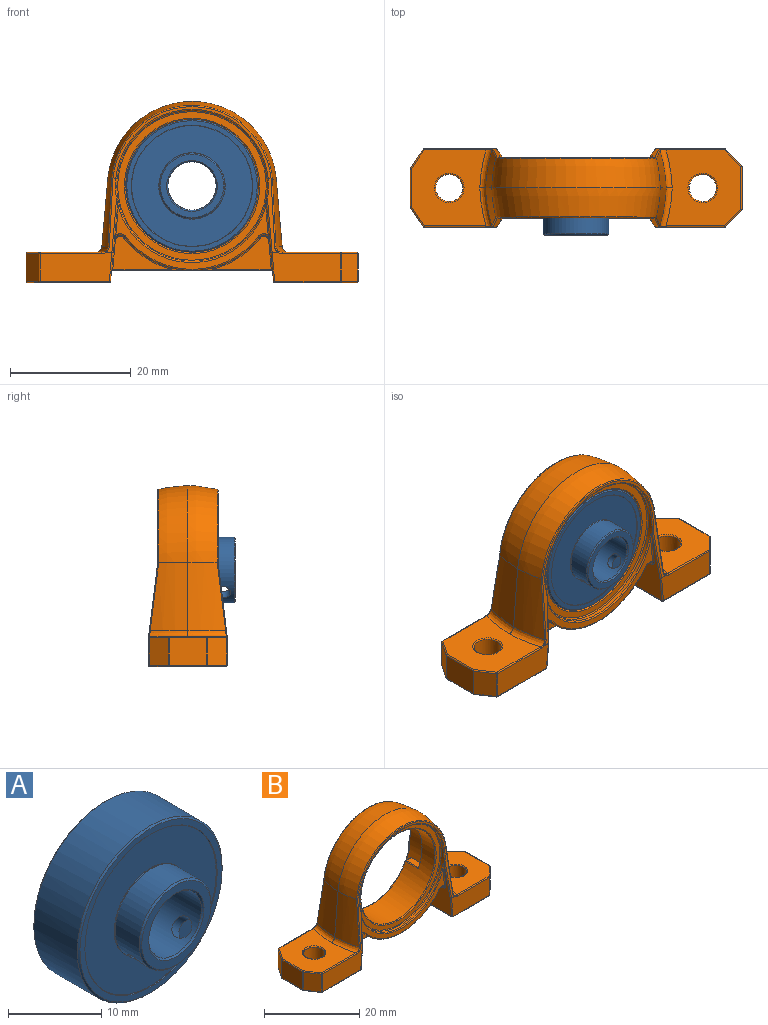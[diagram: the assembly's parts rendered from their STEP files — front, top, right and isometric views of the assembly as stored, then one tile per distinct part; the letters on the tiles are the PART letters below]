
ASSEMBLY  parts=2 mates=1
PART A: 24 faces, bbox 22x10.9x22 mm
  f0: plane 20x20mm, normal (0,1,0), area 219.1mm2, adj f5,f9
  f1: cylinder r=11mm len=22mm, axis (0,1,0), area 456.2mm2, adj f22,f23
  f2: plane 21.6x21.6mm, normal (0,-1,0), area 49.1mm2, adj f6,f22
  f3: plane 21.6x21.6mm, normal (0,1,0), area 49.1mm2, adj f4,f23
  f4: cone r=10.05mm half-angle=45deg, axis (0,1,0), area 4.5mm2, adj f3,f5
  f5: cylinder r=10mm len=20mm, axis (0,1,0), area 3.1mm2, adj f0,f4
  f6: cone r=10.05mm half-angle=45deg, axis (0,-1,0), area 4.5mm2, adj f2,f7
  f7: cylinder r=10mm len=20mm, axis (0,-1,0), area 3.1mm2, adj f6,f8
  f8: plane 20x20mm, normal (0,-1,0), area 219.1mm2, adj f7,f12
  f9: cylinder r=5.5mm len=11mm, axis (0,-1,0), area 1.7mm2, adj f0,f10
  f10: cone r=5.5mm half-angle=45deg, axis (0,-1,0), area 2.4mm2, adj f9,f11
  f11: plane 10.9x10.9mm, normal (0,1,0), area 37.9mm2, adj f10,f19
  f12: cylinder r=5.5mm len=11mm, axis (0,-1,0), area 1.7mm2, adj f8,f15
  f13: plane 10.5x10.5mm, normal (0,-1,0), area 31.2mm2, adj f20,f21
  f14: cylinder r=5.45mm len=10.9mm, axis (0,-1,0), area 115.1mm2, adj f15,f17,f18,f20
  f15: cone r=5.45mm half-angle=45deg, axis (0,1,0), area 2.4mm2, adj f12,f14
  f16: cylinder r=4mm len=10.45mm, axis (0,-1,0), area 252.7mm2, adj f17,f18,f19,f21
  f17: cylinder r=1.25mm len=2.95mm, axis (-0.72,0,-0.69), area 11.6mm2, adj f14,f16
  f18: cylinder r=1.25mm len=2.95mm, axis (0.72,0,-0.69), area 11.6mm2, adj f14,f16
  f19: cone r=4.2mm half-angle=45deg, axis (0,1,0), area 7.3mm2, adj f11,f16
  f20: cone r=5.25mm half-angle=45deg, axis (0,1,0), area 9.5mm2, adj f13,f14
  f21: cone r=4mm half-angle=45deg, axis (0,-1,0), area 7.3mm2, adj f13,f16
  f22: cone r=11mm half-angle=45deg, axis (0,1,0), area 19.4mm2, adj f1,f2
  f23: cone r=10.8mm half-angle=45deg, axis (0,-1,0), area 19.4mm2, adj f1,f3
PART B: 247 faces, bbox 55.2x14x30.2 mm
  f0: plane 22.96x7.55mm, normal (0,1,0), area 35.1mm2, adj f36,f150,f153,f155
  f1: plane 13.6x12.6mm, normal (0,0,-1), area 145.8mm2, adj f133,f134,f135,f136,f137,f138,f139
  f2: plane 12.6x12.38mm, normal (0,0,1), area 122.3mm2, adj f57,f58,f118,f119,f120,f121,f122,f147
  f3: plane 11.31x4.79mm, normal (0,1,0), area 51.3mm2, adj f124,f125,f145,f196,f202,f233
  f4: plane 11.9x4.79mm, normal (0,1,0), area 54mm2, adj f117,f118,f135,f195,f199,f230
  f5: plane 13.6x12.6mm, normal (0,0,-1), area 145.2mm2, adj f140,f141,f142,f143,f144,f145,f146
  f6: plane 7.18x4.6mm, normal (1,0,0), area 33mm2, adj f127,f141,f236,f239
  f7: plane 12.6x12.38mm, normal (0,0,1), area 121.7mm2, adj f55,f56,f125,f126,f127,f128,f129,f148
  f8: plane 6.22x4.6mm, normal (-1,0,0), area 28.6mm2, adj f120,f138,f224,f227
  f9: plane 26.19x11.92mm, normal (0,1,0), area 17mm2, adj f209,f217,f218,f222
  f10: plane 12.19x1.74mm, normal (0,0.99,0.12), area 7.6mm2, adj f199,f200,f207,f208,f212,f217
  f11: plane 12.19x1.74mm, normal (0,0.99,0.12), area 7.6mm2, adj f201,f202,f210,f211,f215,f218,f219
  f12: cylinder r=14mm len=22.23mm, axis (0,-1,0), area 92.4mm2, adj f51,f53,f64,f65,f69,f70,f107
  f13: plane 13.76x12.77mm, normal (-1,0,-0.09), area 79.2mm2, adj f51,f52,f74,f78,f80,f81,f84,f94
  f14: plane 13.76x12.77mm, normal (1,0,-0.09), area 79.2mm2, adj f53,f54,f77,f79,f82,f85,f89,f100
  f15: plane 25.25x10.33mm, normal (0,1,0), area 37.6mm2, adj f105,f107,f109,f110,f113,f114
  f16: cylinder r=11mm len=22mm, axis (0,1,0), area 448.7mm2, adj f47,f50,f132,f149,f152,f153,f157,f160
  f17: plane 26.19x11.92mm, normal (0,-1,0), area 17mm2, adj f179,f187,f188,f192
  f18: plane 11.31x4.79mm, normal (0,-1,0), area 51.3mm2, adj f129,f130,f144,f165,f169,f242
  f19: plane 11.9x4.79mm, normal (0,-1,0), area 54mm2, adj f122,f123,f134,f166,f172,f245
  f20: plane 12.19x1.74mm, normal (0,-0.99,0.12), area 7.6mm2, adj f171,f172,f180,f181,f185,f188
  f21: plane 12.19x1.74mm, normal (0,-0.99,0.12), area 7.6mm2, adj f169,f170,f177,f178,f182,f186,f187
  f22: cylinder r=14mm len=22.23mm, axis (0,1,0), area 92.4mm2, adj f52,f54,f62,f63,f86,f92,f95
  f23: plane 25.25x10.33mm, normal (0,-1,0), area 37.6mm2, adj f93,f95,f97,f98,f101,f102
  f24: cylinder r=12.5mm len=25mm, axis (0,-1,0), area 48.8mm2, adj f96,f99,f101,f103,f104,f131,f178,f179
  f25: plane 24.6x24.6mm, normal (0,-1,0), area 81.2mm2, adj f131,f132
  f26: plane 26.31x1.6mm, normal (0,0,-1), area 42.1mm2, adj f59,f60,f67,f68,f75,f76,f81,f82
  f27: plane 9.77x5.48mm, normal (0,-1,0), area 24mm2, adj f88,f89,f91,f92
  f28: plane 9.77x5.48mm, normal (0,-1,0), area 24mm2, adj f80,f83,f86,f87
  f29: cylinder r=25.08mm len=11.46mm, axis (-0.09,0,-1), area 63.8mm2, adj f31,f40,f57,f185,f189
  f30: cylinder r=25.08mm len=11.4mm, axis (-0.09,0,1), area 63.5mm2, adj f31,f41,f55,f182
  f31: revolved ~27.89x12.9mm, area 199.8mm2, adj f29,f30,f42,f186,f190,f191,f192
  f32: cylinder r=2.25mm len=4.6mm, axis (0,0,1), area 65mm2, adj f139,f147
  f33: plane 4.6x3.19mm, normal (-0.83,-0.55,0), area 17.6mm2, adj f121,f136,f224,f245
  f34: plane 4.6x2.71mm, normal (0.71,-0.71,0), area 17.6mm2, adj f128,f142,f239,f242
  f35: cylinder r=2.25mm len=4.6mm, axis (0,0,1), area 65mm2, adj f140,f148
  f36: cylinder r=12.5mm len=25mm, axis (0,1,0), area 142.5mm2, adj f0,f37,f45,f46,f47,f48,f49,f50
  f37: plane 22.96x7.55mm, normal (0,1,0), area 35.1mm2, adj f36,f156,f159,f160
  f38: plane 9.77x5.48mm, normal (0,1,0), area 24mm2, adj f70,f73,f76,f77
  f39: plane 9.77x5.48mm, normal (0,1,0), area 24mm2, adj f69,f71,f74,f75
  f40: cylinder r=25.09mm len=11.46mm, axis (-0.09,0,-1), area 63.8mm2, adj f29,f42,f58,f212,f216
  f41: cylinder r=25.09mm len=11.4mm, axis (-0.09,0,1), area 63.5mm2, adj f30,f42,f56,f215
  f42: revolved ~27.89x12.9mm, area 199.8mm2, adj f31,f40,f41,f219,f220,f221,f222
  f43: plane 4.6x3.19mm, normal (-0.83,0.55,0), area 17.6mm2, adj f119,f137,f227,f230
  f44: plane 4.6x2.71mm, normal (0.71,0.71,0), area 17.6mm2, adj f126,f143,f233,f236
  f45: plane 3.8x1.52mm, normal (0,0,-1), area 5.8mm2, adj f36,f47,f152,f155
  f46: plane 3.8x1.52mm, normal (0,0,1), area 5.8mm2, adj f36,f47,f159,f162
  f47: plane 9.72x2.63mm, normal (0,1,0), area 14.7mm2, adj f16,f36,f45,f46,f152,f162
  f48: plane 3.8x1.52mm, normal (0,0,-1), area 5.8mm2, adj f36,f50,f149,f150
  f49: plane 3.8x1.52mm, normal (0,0,1), area 5.8mm2, adj f36,f50,f156,f157
  f50: plane 9.72x2.63mm, normal (0,1,0), area 14.7mm2, adj f16,f36,f48,f49,f149,f157
  f51: cylinder r=1mm len=3.6mm, axis (0,-1,0), area 8.6mm2, adj f12,f13,f71,f110
  f52: cylinder r=1mm len=3.6mm, axis (0,1,0), area 8.6mm2, adj f13,f22,f83,f93
  f53: cylinder r=1mm len=3.6mm, axis (0,-1,0), area 8.6mm2, adj f12,f14,f73,f105
  f54: cylinder r=1mm len=3.6mm, axis (0,1,0), area 8.6mm2, adj f14,f22,f91,f98
  f55: bspline ~11.42x2.29mm, area 9.5mm2, adj f7,f30,f56,f130,f177
  f56: bspline ~7.28x2.2mm, area 9.5mm2, adj f7,f41,f55,f124,f211
  f57: bspline ~11.42x2.29mm, area 9.5mm2, adj f2,f29,f58,f123,f181
  f58: bspline ~8.05x2.18mm, area 9.5mm2, adj f2,f40,f57,f117,f207
  f59: bspline ~3.35x0.2mm, area 0.6mm2, adj f26,f60,f88,f90
  f60: bspline ~3.35x0.2mm, area 0.6mm2, adj f26,f59,f61,f87
  f61: bspline ~3.35x0.34mm, area 0.4mm2, adj f60,f62,f86,f87
  f62: bspline ~3.31x0.39mm, area 0.5mm2, adj f22,f61,f63,f86
  f63: bspline ~3.31x0.39mm, area 0.5mm2, adj f22,f62,f90,f92
  f64: bspline ~3.31x0.39mm, area 0.5mm2, adj f12,f65,f70,f72
  f65: bspline ~3.31x0.39mm, area 0.5mm2, adj f12,f64,f66,f69
  f66: bspline ~3.35x0.34mm, area 0.4mm2, adj f65,f67,f69,f75
  f67: bspline ~3.35x0.2mm, area 0.6mm2, adj f26,f66,f68,f75
  f68: bspline ~3.35x0.2mm, area 0.6mm2, adj f26,f67,f72,f76
  f69: torus R=14.2mm, axis (0,-1,0), area 3mm2, adj f12,f39,f65,f66,f71
  f70: torus R=14.2mm, axis (0,-1,0), area 3mm2, adj f12,f38,f64,f72,f73
  f71: torus R=0.8mm, axis (0,-1,0), area 0.7mm2, adj f39,f51,f69,f74
  f72: bspline ~3.35x0.34mm, area 0.4mm2, adj f64,f68,f70,f76
  f73: torus R=0.8mm, axis (0,-1,0), area 0.7mm2, adj f38,f53,f70,f77
  f74: cylinder r=0.2mm len=4.76mm, axis (0.09,0,-1), area 1.5mm2, adj f13,f39,f71,f78
  f75: cylinder r=0.2mm len=9.81mm, axis (1,0,0), area 3.1mm2, adj f26,f39,f66,f67,f78
  f76: cylinder r=0.2mm len=9.81mm, axis (1,0,0), area 3.1mm2, adj f26,f38,f68,f72,f79
  f77: cylinder r=0.2mm len=4.76mm, axis (-0.09,0,-1), area 1.5mm2, adj f14,f38,f73,f79
  f78: bspline ~0.4x0.4mm, area 0.1mm2, adj f13,f74,f75,f81
  f79: bspline ~0.47x0.47mm, area 0.1mm2, adj f14,f76,f77,f82
  f80: cylinder r=0.2mm len=4.76mm, axis (0.09,0,-1), area 1.5mm2, adj f13,f28,f83,f84
  f81: cylinder r=0.2mm len=1.6mm, axis (0,1,0), area 0.5mm2, adj f13,f26,f78,f84
  f82: cylinder r=0.2mm len=1.6mm, axis (0,-1,0), area 0.5mm2, adj f14,f26,f79,f85
  f83: torus R=0.8mm, axis (0,1,0), area 0.7mm2, adj f28,f52,f80,f86
  f84: bspline ~0.5x0.4mm, area 0.1mm2, adj f13,f80,f81,f87
  f85: bspline ~0.47x0.42mm, area 0.1mm2, adj f14,f82,f88,f89
  f86: torus R=14.2mm, axis (0,1,0), area 3mm2, adj f22,f28,f61,f62,f83
  f87: cylinder r=0.2mm len=9.81mm, axis (1,0,0), area 3.1mm2, adj f26,f28,f60,f61,f84
  f88: cylinder r=0.2mm len=9.81mm, axis (1,0,0), area 3.1mm2, adj f26,f27,f59,f85,f90
  f89: cylinder r=0.2mm len=4.76mm, axis (-0.09,0,-1), area 1.5mm2, adj f14,f27,f85,f91
  f90: bspline ~3.35x0.34mm, area 0.4mm2, adj f59,f63,f88,f92
  f91: torus R=0.8mm, axis (0,1,0), area 0.7mm2, adj f27,f54,f89,f92
  f92: torus R=14.2mm, axis (0,1,0), area 3mm2, adj f22,f27,f63,f90,f91
  f93: torus R=1.2mm, axis (0,-1,0), area 0.7mm2, adj f23,f52,f94,f95
  f94: bspline ~1.03x0.4mm, area 0.1mm2, adj f13,f93,f97
  f95: torus R=13.8mm, axis (0,-1,0), area 8mm2, adj f22,f23,f93,f98
  f96: cylinder r=0.2mm len=0.05mm, axis (0,-1,0), area 0mm2, adj f13,f24,f99,f174
  f97: cylinder r=0.2mm len=5.94mm, axis (-0.09,0,1), area 1.7mm2, adj f13,f23,f94,f99
  f98: torus R=1.2mm, axis (0,-1,0), area 0.7mm2, adj f23,f54,f95,f100
  f99: bspline ~1.39x0.42mm, area 0.3mm2, adj f24,f96,f97,f101
  f100: bspline ~1.03x0.4mm, area 0.1mm2, adj f14,f98,f102
  f101: torus R=12.7mm, axis (0,-1,0), area 10.2mm2, adj f23,f24,f99,f103
  f102: cylinder r=0.2mm len=5.94mm, axis (-0.09,0,-1), area 1.7mm2, adj f14,f23,f100,f103
  f103: bspline ~1.39x0.43mm, area 0.3mm2, adj f24,f101,f102,f104
  f104: cylinder r=0.2mm len=0.05mm, axis (0,-1,0), area 0mm2, adj f14,f24,f103,f175
  f105: torus R=1.2mm, axis (0,1,0), area 0.7mm2, adj f15,f53,f106,f107
  f106: bspline ~1.03x0.4mm, area 0.1mm2, adj f14,f105,f109
  f107: torus R=13.8mm, axis (0,1,0), area 8mm2, adj f12,f15,f105,f110
  f108: cylinder r=0.2mm len=0.05mm, axis (0,1,0), area 0mm2, adj f14,f36,f111,f204
  f109: cylinder r=0.2mm len=5.94mm, axis (-0.09,0,-1), area 1.7mm2, adj f14,f15,f106,f111
  f110: torus R=1.2mm, axis (0,1,0), area 0.7mm2, adj f15,f51,f107,f112
  f111: bspline ~1.39x0.42mm, area 0.3mm2, adj f36,f108,f109,f113
  f112: bspline ~1.03x0.4mm, area 0.1mm2, adj f13,f110,f114
  f113: torus R=12.7mm, axis (0,1,0), area 10.2mm2, adj f15,f36,f111,f115
  f114: cylinder r=0.2mm len=5.94mm, axis (-0.09,0,1), area 1.7mm2, adj f13,f15,f112,f115
  f115: bspline ~1.39x0.43mm, area 0.3mm2, adj f36,f113,f114,f116
  f116: cylinder r=0.2mm len=0.05mm, axis (0,1,0), area 0mm2, adj f13,f36,f115,f205
  f117: bspline ~1.15x0.47mm, area 0.2mm2, adj f4,f58,f118,f203
  f118: cylinder r=0.2mm len=10.25mm, axis (-1,0,0), area 3.2mm2, adj f2,f4,f117,f229
  f119: cylinder r=0.2mm len=3.3mm, axis (0.55,0.83,0), area 1.2mm2, adj f2,f43,f226,f229
  f120: cylinder r=0.2mm len=6.22mm, axis (0,1,0), area 2mm2, adj f2,f8,f223,f226
  f121: cylinder r=0.2mm len=3.3mm, axis (-0.55,0.83,0), area 1.2mm2, adj f2,f33,f223,f244
  f122: cylinder r=0.2mm len=10.25mm, axis (-1,0,0), area 3.2mm2, adj f2,f19,f123,f244
  f123: bspline ~1.15x0.47mm, area 0.2mm2, adj f19,f57,f122,f176
  f124: bspline ~1.15x0.47mm, area 0.2mm2, adj f3,f56,f125,f206
  f125: cylinder r=0.2mm len=9.67mm, axis (-1,0,0), area 3mm2, adj f3,f7,f124,f232
  f126: cylinder r=0.2mm len=2.85mm, axis (-0.71,0.71,0), area 1.2mm2, adj f7,f44,f232,f235
  f127: cylinder r=0.2mm len=7.18mm, axis (0,1,0), area 2.3mm2, adj f6,f7,f235,f238
  f128: cylinder r=0.2mm len=2.85mm, axis (0.71,0.71,0), area 1.2mm2, adj f7,f34,f238,f241
  f129: cylinder r=0.2mm len=9.67mm, axis (-1,0,0), area 3mm2, adj f7,f18,f130,f241
  f130: bspline ~1.15x0.47mm, area 0.2mm2, adj f18,f55,f129,f173
  f131: torus R=12.3mm, axis (0,-1,0), area 24.5mm2, adj f24,f25
  f132: torus R=11.2mm, axis (0,-1,0), area 21.9mm2, adj f16,f25
  f133: cylinder r=0.2mm len=12.6mm, axis (0,-1,0), area 3.7mm2, adj f1,f14,f164,f193
  f134: cylinder r=0.2mm len=11.48mm, axis (1,0,0), area 3.6mm2, adj f1,f19,f164,f246
  f135: cylinder r=0.2mm len=11.48mm, axis (1,0,0), area 3.6mm2, adj f1,f4,f193,f231
  f136: cylinder r=0.2mm len=3.3mm, axis (-0.55,0.83,0), area 1.2mm2, adj f1,f33,f225,f246
  f137: cylinder r=0.2mm len=3.3mm, axis (0.55,0.83,0), area 1.2mm2, adj f1,f43,f228,f231
  f138: cylinder r=0.2mm len=6.22mm, axis (0,1,0), area 2mm2, adj f1,f8,f225,f228
  f139: torus R=2.45mm, axis (0,0,1), area 4.6mm2, adj f1,f32
  f140: torus R=2.45mm, axis (0,0,-1), area 4.6mm2, adj f5,f35
  f141: cylinder r=0.2mm len=7.18mm, axis (0,1,0), area 2.3mm2, adj f5,f6,f237,f240
  f142: cylinder r=0.2mm len=2.85mm, axis (0.71,0.71,0), area 1.2mm2, adj f5,f34,f240,f243
  f143: cylinder r=0.2mm len=2.85mm, axis (-0.71,0.71,0), area 1.2mm2, adj f5,f44,f234,f237
  f144: cylinder r=0.2mm len=10.89mm, axis (1,0,0), area 3.4mm2, adj f5,f18,f163,f243
  f145: cylinder r=0.2mm len=10.89mm, axis (1,0,0), area 3.4mm2, adj f3,f5,f194,f234
  f146: cylinder r=0.2mm len=12.6mm, axis (0,-1,0), area 3.7mm2, adj f5,f13,f163,f194
  f147: torus R=2.45mm, axis (0,0,-1), area 4.6mm2, adj f2,f32
  f148: torus R=2.45mm, axis (0,0,1), area 4.6mm2, adj f7,f35
  f149: cylinder r=0.2mm len=3.8mm, axis (0,1,0), area 0.8mm2, adj f16,f48,f50,f151
  f150: cylinder r=0.2mm len=1.52mm, axis (-1,0,0), area 0.5mm2, adj f0,f36,f48,f151
  f151: sphere r=0.2mm, area 0mm2, adj f149,f150,f153
  f152: cylinder r=0.2mm len=3.8mm, axis (0,1,0), area 0.8mm2, adj f16,f45,f47,f154
  f153: torus R=11.2mm, axis (0,1,0), area 7.7mm2, adj f0,f16,f151,f154
  f154: sphere r=0.2mm, area 0mm2, adj f152,f153,f155
  f155: cylinder r=0.2mm len=1.52mm, axis (-1,0,0), area 0.5mm2, adj f0,f36,f45,f154
  f156: cylinder r=0.2mm len=1.52mm, axis (1,0,0), area 0.5mm2, adj f36,f37,f49,f158
  f157: cylinder r=0.2mm len=3.8mm, axis (0,1,0), area 0.8mm2, adj f16,f49,f50,f158
  f158: sphere r=0.2mm, area 0mm2, adj f156,f157,f160
  f159: cylinder r=0.2mm len=1.52mm, axis (1,0,0), area 0.5mm2, adj f36,f37,f46,f161
  f160: torus R=11.2mm, axis (0,1,0), area 7.7mm2, adj f16,f37,f158,f161
  f161: sphere r=0.2mm, area 0mm2, adj f159,f160,f162
  f162: cylinder r=0.2mm len=3.8mm, axis (0,1,0), area 0.8mm2, adj f16,f46,f47,f161
  f163: sphere r=0.2mm, area 0.1mm2, adj f144,f146,f165
  f164: sphere r=0.2mm, area 0.1mm2, adj f133,f134,f166
  f165: cylinder r=0.2mm len=4.81mm, axis (0.09,0,-1), area 1.5mm2, adj f13,f18,f163,f167
  f166: cylinder r=0.2mm len=4.81mm, axis (0.09,0,1), area 1.5mm2, adj f14,f19,f164,f168
  f167: sphere r=0.2mm, area 0mm2, adj f165,f169,f170
  f168: sphere r=0.2mm, area 0mm2, adj f166,f171,f172
  f169: cylinder r=0.2mm len=0.97mm, axis (-1,0,0), area 0mm2, adj f18,f21,f167,f173
  f170: cylinder r=0.2mm len=8.84mm, axis (-0.09,0.12,0.99), area 2.8mm2, adj f13,f21,f167,f174
  f171: cylinder r=0.2mm len=8.84mm, axis (-0.09,-0.12,-0.99), area 2.8mm2, adj f14,f20,f168,f175
  f172: cylinder r=0.2mm len=0.97mm, axis (1,0,0), area 0mm2, adj f19,f20,f168,f176
  f173: sphere r=0.2mm, area 0mm2, adj f130,f169,f177
  f174: sphere r=0.2mm, area 0mm2, adj f96,f170,f178
  f175: sphere r=0.2mm, area 0mm2, adj f104,f171,f180
  f176: sphere r=0.2mm, area 0mm2, adj f123,f172,f181
  f177: bspline ~1.15x0.73mm, area 0.3mm2, adj f21,f55,f173,f182
  f178: bspline ~3.39x0.62mm, area 1.1mm2, adj f21,f24,f174,f183
  f179: torus R=12.7mm, axis (0,-1,0), area 11.6mm2, adj f17,f24,f183,f184
  f180: bspline ~3.39x0.62mm, area 1.1mm2, adj f20,f24,f175,f184
  f181: bspline ~1.13x0.79mm, area 0.3mm2, adj f20,f57,f176,f185
  f182: bspline ~13.27x1.78mm, area 2.9mm2, adj f21,f30,f177,f186
  f183: bspline ~0.22x0.22mm, area 0mm2, adj f24,f178,f179,f187
  f184: bspline ~0.22x0.21mm, area 0mm2, adj f24,f179,f180,f188
  f185: bspline ~13.27x1.78mm, area 3mm2, adj f20,f29,f181,f189
  f186: bspline ~3.79x0.63mm, area 0mm2, adj f21,f31,f182,f190
  f187: cylinder r=0.2mm len=0.45mm, axis (1,0,0), area 0mm2, adj f17,f21,f183,f190
  f188: cylinder r=0.2mm len=0.45mm, axis (1,0,0), area 0mm2, adj f17,f20,f184,f189,f191
  f189: bspline ~0.2x0.16mm, area 0mm2, adj f29,f185,f188,f191
  f190: bspline ~0.21x0.17mm, area 0mm2, adj f31,f186,f187,f192
  f191: bspline ~0.21x0.18mm, area 0mm2, adj f31,f188,f189,f192
  f192: bspline ~26.56x12.1mm, area 10.5mm2, adj f17,f31,f190,f191
  f193: sphere r=0.2mm, area 0mm2, adj f133,f135,f195
  f194: sphere r=0.2mm, area 0.1mm2, adj f145,f146,f196
  f195: cylinder r=0.2mm len=4.81mm, axis (0.09,0,1), area 1.5mm2, adj f4,f14,f193,f197
  f196: cylinder r=0.2mm len=4.81mm, axis (0.09,0,-1), area 1.5mm2, adj f3,f13,f194,f198
  f197: sphere r=0.2mm, area 0mm2, adj f195,f199,f200
  f198: sphere r=0.2mm, area 0mm2, adj f196,f201,f202
  f199: cylinder r=0.2mm len=0.97mm, axis (1,0,0), area 0mm2, adj f4,f10,f197,f203
  f200: cylinder r=0.2mm len=8.84mm, axis (-0.09,0.12,-0.99), area 2.8mm2, adj f10,f14,f197,f204
  f201: cylinder r=0.2mm len=8.84mm, axis (-0.09,-0.12,0.99), area 2.8mm2, adj f11,f13,f198,f205
  f202: cylinder r=0.2mm len=0.97mm, axis (-1,0,0), area 0mm2, adj f3,f11,f198,f206
  f203: sphere r=0.2mm, area 0mm2, adj f117,f199,f207
  f204: sphere r=0.2mm, area 0mm2, adj f108,f200,f208
  f205: sphere r=0.2mm, area 0mm2, adj f116,f201,f210
  f206: sphere r=0.2mm, area 0mm2, adj f124,f202,f211
  f207: bspline ~1.15x0.73mm, area 0.3mm2, adj f10,f58,f203,f212
  f208: bspline ~3.39x0.62mm, area 1.1mm2, adj f10,f36,f204,f213
  f209: torus R=12.7mm, axis (0,1,0), area 11.6mm2, adj f9,f36,f213,f214
  f210: bspline ~3.39x0.62mm, area 1.1mm2, adj f11,f36,f205,f214
  f211: bspline ~1.13x0.79mm, area 0.3mm2, adj f11,f56,f206,f215
  f212: bspline ~13.27x1.78mm, area 3mm2, adj f10,f40,f207,f216
  f213: bspline ~0.22x0.22mm, area 0mm2, adj f36,f208,f209,f217
  f214: bspline ~0.22x0.21mm, area 0mm2, adj f36,f209,f210,f218
  f215: bspline ~11.2x1.53mm, area 2.9mm2, adj f11,f41,f211,f219
  f216: bspline ~0.2x0.16mm, area 0mm2, adj f40,f212,f217,f220
  f217: cylinder r=0.2mm len=0.45mm, axis (-1,0,0), area 0mm2, adj f9,f10,f213,f216,f220
  f218: cylinder r=0.2mm len=0.45mm, axis (-1,0,0), area 0mm2, adj f9,f11,f214,f221
  f219: bspline ~3.79x0.63mm, area 0mm2, adj f11,f42,f215,f221
  f220: bspline ~0.21x0.18mm, area 0mm2, adj f42,f216,f217,f222
  f221: bspline ~0.2x0.17mm, area 0mm2, adj f42,f218,f219,f222
  f222: bspline ~26.66x12.66mm, area 10.5mm2, adj f9,f42,f220,f221
  f223: sphere r=0.2mm, area 0mm2, adj f120,f121,f224
  f224: cylinder r=0.2mm len=4.6mm, axis (0,0,1), area 0.5mm2, adj f8,f33,f223,f225
  f225: sphere r=0.2mm, area 0mm2, adj f136,f138,f224
  f226: sphere r=0.2mm, area 0mm2, adj f119,f120,f227
  f227: cylinder r=0.2mm len=4.6mm, axis (0,0,-1), area 0.5mm2, adj f8,f43,f226,f228
  f228: sphere r=0.2mm, area 0mm2, adj f137,f138,f227
  f229: sphere r=0.2mm, area 0mm2, adj f118,f119,f230
  f230: cylinder r=0.2mm len=4.6mm, axis (0,0,-1), area 0.9mm2, adj f4,f43,f229,f231
  f231: sphere r=0.2mm, area 0mm2, adj f135,f137,f230
  f232: sphere r=0.2mm, area 0mm2, adj f125,f126,f233
  f233: cylinder r=0.2mm len=4.6mm, axis (0,0,-1), area 0.7mm2, adj f3,f44,f232,f234
  f234: sphere r=0.2mm, area 0mm2, adj f143,f145,f233
  f235: sphere r=0.2mm, area 0mm2, adj f126,f127,f236
  f236: cylinder r=0.2mm len=4.6mm, axis (0,0,1), area 0.7mm2, adj f6,f44,f235,f237
  f237: sphere r=0.2mm, area 0mm2, adj f141,f143,f236
  f238: sphere r=0.2mm, area 0mm2, adj f127,f128,f239
  f239: cylinder r=0.2mm len=4.6mm, axis (0,0,-1), area 0.7mm2, adj f6,f34,f238,f240
  f240: sphere r=0.2mm, area 0mm2, adj f141,f142,f239
  f241: sphere r=0.2mm, area 0mm2, adj f128,f129,f242
  f242: cylinder r=0.2mm len=4.6mm, axis (0,0,1), area 0.7mm2, adj f18,f34,f241,f243
  f243: sphere r=0.2mm, area 0mm2, adj f142,f144,f242
  f244: sphere r=0.2mm, area 0mm2, adj f121,f122,f245
  f245: cylinder r=0.2mm len=4.6mm, axis (0,0,1), area 0.9mm2, adj f19,f33,f244,f246
  f246: sphere r=0.2mm, area 0mm2, adj f134,f136,f245
PLACE A t=(0,3,0)mm
PLACE B at identity
MATE revolute A.f1 <-> B.f12  axis (0,-1,0) through (0,-4,0)mm
